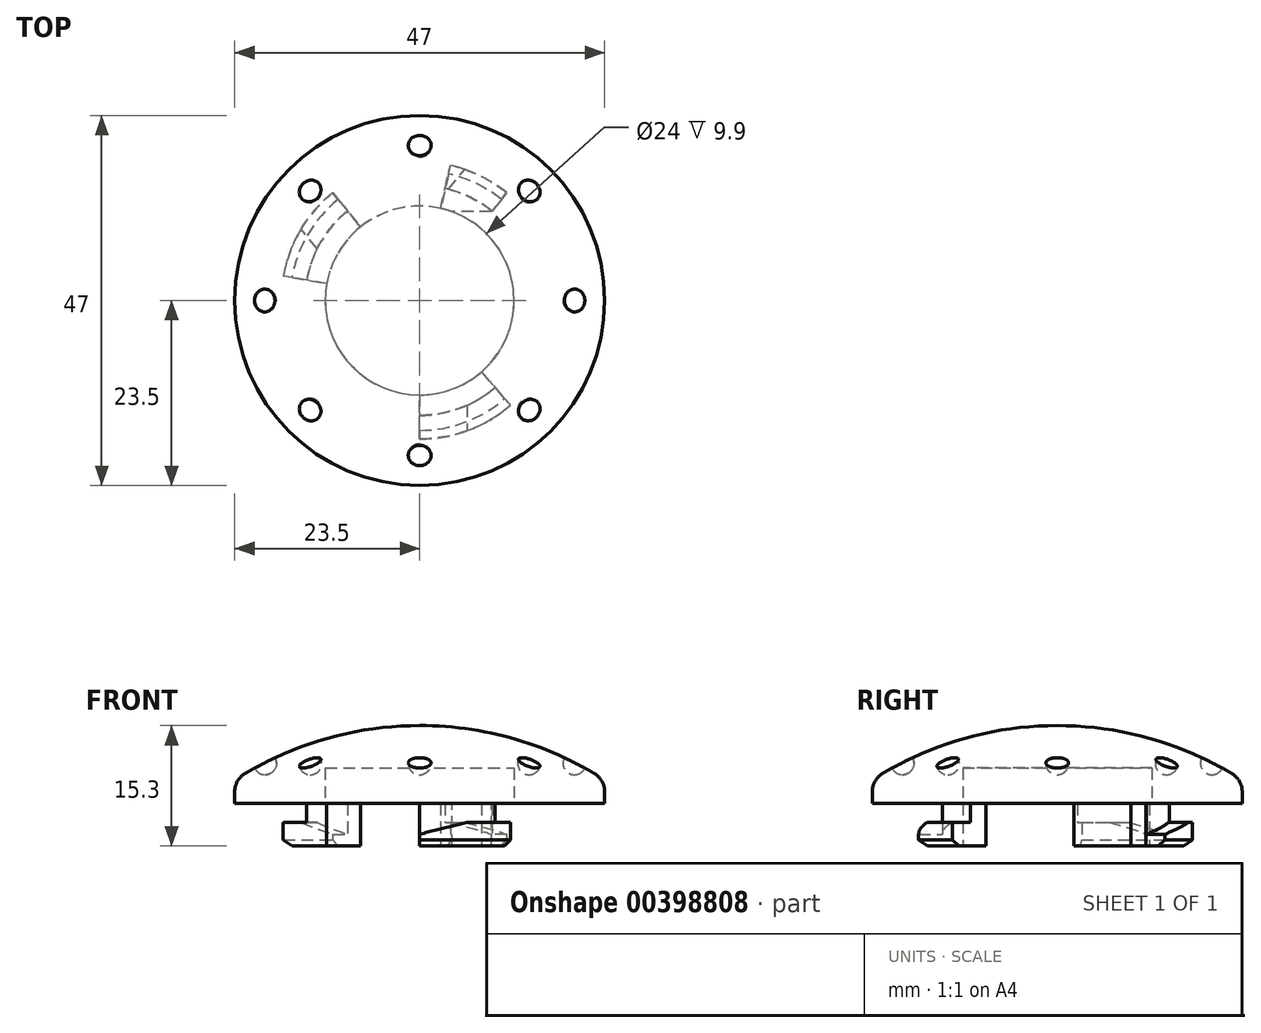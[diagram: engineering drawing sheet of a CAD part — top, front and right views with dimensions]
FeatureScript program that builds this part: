
annotation { "Feature Type Name" : "Feature", "Feature Type Description" : "" }
export const myFeature = defineFeature(function(context is Context, id is Id, definition is map)
    precondition{}
    {
        {
            var Q0;
            Q0=qCreatedBy(makeId("Front.planeOp"),FACE);
            var sketch = newSketch(context, id + "F0", { "sketchPlane" : qUnion([Q0])});
            skLineSegment(sketch, "E0", {"start": v(14.6, 0) * mm, "end": v(23.5, 0) * mm});
            skLineSegment(sketch, "E1", {"start": v(23.5, 0) * mm, "end": v(23.5, 3) * mm});
            skArc(sketch, "E2", {"start": v(23.5, 3) * mm, "mid": v(12.25, 8.14) * mm, "end": v(0, 9.9) * mm});
            skLineSegment(sketch, "E3", {"start": v(0, 4.5) * mm, "end": v(0, 9.9) * mm});
            skLineSegment(sketch, "E4", {"start": v(0, 4.5) * mm, "end": v(12, 4.5) * mm});
            skLineSegment(sketch, "E5", {"start": v(12, 4.5) * mm, "end": v(12, 0) * mm});
            skPoint(sketch, "E6.orphan", {"position": v(0, 0) * mm});
            skLineSegment(sketch, "E7", {"start": v(12, 0) * mm, "end": v(12, -5.4) * mm});
            skLineSegment(sketch, "E8", {"start": v(12, -5.4) * mm, "end": v(16.5, -5.4) * mm});
            skLineSegment(sketch, "E9", {"start": v(16.5, -5.4) * mm, "end": v(17.6, -4.6) * mm});
            skLineSegment(sketch, "E10", {"start": v(17.6, -4.6) * mm, "end": v(17.6, -2.4) * mm});
            skLineSegment(sketch, "E11", {"start": v(17.6, -2.4) * mm, "end": v(14.6, -2.4) * mm});
            skLineSegment(sketch, "E12", {"start": v(14.6, -2.4) * mm, "end": v(14.6, 0) * mm});
            skSolve(sketch);
        }
        {
            var Q0;
            Q0=makeQuery(id+"F0.imprint","IMPRINT",FACE,{"disambiguationData":[TD([[makeQuery(id+"F0.imprint","IMPRINT",EDGE,{"derivedFrom":sQuery(id+"F0.wireOp",EDGE,"E0")}),1.0]])]});
            var Q1;
            Q1=sQuery(id+"F0.wireOp",EDGE,"E3");
            revolve(context, id + "F1", {"entities" : qUnion([Q0]), "axis" : qUnion([Q1]), "revolveType" : RevolveType.FULL});
        }
        {
            var Q0;
            Q0=makeQuery(id+"F1.opRevolve","SWEPT_EDGE",EDGE,{"disambiguationData":[OSD([sQuery(id+"F0.wireOp",EDGE,"E1"),sQuery(id+"F0.wireOp",EDGE,"E2")])]});
            fillet(context, id + "F2", {"entities" : qUnion([Q0]), "radius" : 2.7 * mm, "tangentPropagation" : true, "allowEdgeOverflow" : false});
        }
        {
            var Q0;
            Q0=qCreatedBy(makeId("Top.planeOp"),FACE);
            var sketch = newSketch(context, id + "F3", { "sketchPlane" : qUnion([Q0])});
            skCircle(sketch, "E13", {"center": v(0, 0) * mm, "radius": 14.6 * mm, "construction": true});
            skLineSegment(sketch, "E14", {"start": v(0, 0) * mm, "end": v(0, -14.6) * mm, "construction": true});
            skLineSegment(sketch, "E15", {"start": v(0, 0) * mm, "end": v(9.56, -11.04) * mm, "construction": true});
            skLineSegment(sketch, "E16", {"start": v(0, 0) * mm, "end": v(-14.37, 2.58) * mm, "construction": true});
            skLineSegment(sketch, "E17", {"start": v(0, 0) * mm, "end": v(-9.17, 11.36) * mm, "construction": true});
            skLineSegment(sketch, "E18", {"start": v(9.1, 11.28) * mm, "end": v(9.17, 11.36) * mm, "construction": true});
            skLineSegment(sketch, "E19", {"start": v(0, 0) * mm, "end": v(3.23, 14.24) * mm, "construction": true});
            skArc(sketch, "E20", {"start": v(15.38, -17.77) * mm, "mid": v(23.5, 0.4) * mm, "end": v(14.76, 18.28) * mm});
            skLineSegment(sketch, "E21", {"start": v(0, 0) * mm, "end": v(-23.13, 4.16) * mm});
            skLineSegment(sketch, "E22", {"start": v(0, 0) * mm, "end": v(0, -23.5) * mm});
            skLineSegment(sketch, "E23", {"start": v(0, 0) * mm, "end": v(15.38, -17.77) * mm});
            skLineSegment(sketch, "E24", {"start": v(9.1, 11.28) * mm, "end": v(14.76, 18.28) * mm});
            skLineSegment(sketch, "E25", {"start": v(0, 0) * mm, "end": v(5.2, 22.92) * mm});
            skLineSegment(sketch, "E26", {"start": v(0, 0) * mm, "end": v(-14.76, 18.28) * mm});
            skArc(sketch, "E27.trimOffspring", {"start": v(5.2, 22.92) * mm, "mid": v(-5.31, 22.9) * mm, "end": v(-14.76, 18.28) * mm});
            skArc(sketch, "E28.trimOffspring", {"start": v(-23.13, 4.16) * mm, "mid": v(-18.03, -15.08) * mm, "end": v(0, -23.5) * mm});
            skLineSegment(sketch, "E29", {"start": v(4.09, 11.28) * mm, "end": v(9.1, 11.28) * mm});
            skLineSegment(sketch, "E30", {"start": v(4.09, 11.28) * mm, "end": v(0, 0) * mm});
            skSolve(sketch);
        }
        {
            var Q0;
            Q0 = qSketchRegion(id + "F3", true);
            extrude(context, id + "F4", {"entities" : qUnion([Q0]), "operationType" : NewBodyOperationType.REMOVE, "endBound" : BoundingType.THROUGH_ALL, "oppositeDirection" : true, "depth" : 25 * mm});
        }
        {
            var Q0;
            Q0=qCreatedBy(makeId("Front.planeOp"),FACE);
            var sketch = newSketch(context, id + "F5", { "sketchPlane" : qUnion([Q0])});
            skArc(sketch, "E31", {"start": v(19.65, 3.65) * mm, "mid": v(21.1, 5.1) * mm, "end": v(19.65, 6.55) * mm});
            skLineSegment(sketch, "E32", {"start": v(19.65, 3.65) * mm, "end": v(19.65, 6.55) * mm});
            skSolve(sketch);
        }
        {
            var Q0;
            Q0=makeQuery(id+"F5.imprint","IMPRINT",FACE,{"disambiguationData":[TD([[makeQuery(id+"F5.imprint","IMPRINT",EDGE,{"derivedFrom":sQuery(id+"F5.wireOp",EDGE,"E31")}),1.0]])]});
            var Q1;
            Q1=sQuery(id+"F5.wireOp",EDGE,"E32");
            revolve(context, id + "F6", {"entities" : qUnion([Q0]), "axis" : qUnion([Q1]), "revolveType" : RevolveType.FULL});
        }
        {
            var Q0;
            Q0=makeQuery(id+"F6.opRevolve","SWEPT_BODY",BODY,{"disambiguationData":[OSD([sQuery(id+"F5.wireOp",EDGE,"E31"),sQuery(id+"F5.wireOp",EDGE,"E32")])]});
            var Q1;
            Q1=sQuery(id+"F0.wireOp",EDGE,"E3");
            circularPattern(context, id + "F7", {"operationType" : NewBodyOperationType.REMOVE, "entities" : qUnion([Q0]), "axis" : qUnion([Q1]), "angle" : 360 * degree, "instanceCount" : 8, "equalSpace" : true});
        }
        {
            var Q0;
            Q0=makeQuery(id+"F4.boolean.opBoolean","INTERSECT",EDGE,{"derivedFrom":[makeQuery(id+"F1.opRevolve","SWEPT_FACE",FACE,{"disambiguationData":[OSD([sQuery(id+"F0.wireOp",EDGE,"E11")])]}),makeQuery(id+"F4.opExtrude","SWEPT_FACE",FACE,{"disambiguationData":[OSD([sQuery(id+"F3.wireOp",EDGE,"E22")])]})]});
            var Q1;
            Q1=makeQuery(id+"F4.boolean.opBoolean","INTERSECT",EDGE,{"derivedFrom":[makeQuery(id+"F1.opRevolve","SWEPT_FACE",FACE,{"disambiguationData":[OSD([sQuery(id+"F0.wireOp",EDGE,"E11")])]}),makeQuery(id+"F4.opExtrude","SWEPT_FACE",FACE,{"disambiguationData":[OSD([sQuery(id+"F3.wireOp",EDGE,"E26")])]})]});
            var Q2;
            Q2=makeQuery(id+"F4.boolean.opBoolean","INTERSECT",EDGE,{"derivedFrom":[makeQuery(id+"F1.opRevolve","SWEPT_FACE",FACE,{"disambiguationData":[OSD([sQuery(id+"F0.wireOp",EDGE,"E11")])]}),makeQuery(id+"F4.opExtrude","SWEPT_FACE",FACE,{"disambiguationData":[OSD([sQuery(id+"F3.wireOp",EDGE,"E24")])]})]});
            chamfer(context, id + "F8", {"entities" : qUnion([Q0, Q1, Q2]), "chamferType" : ChamferType.TWO_OFFSETS, "width1" : 6 * mm, "oppositeDirection" : false, "width2" : 1.5 * mm, "tangentPropagation" : true});
        }
    });
